# Revit family: Caja de conexión CBO 5-SEC_Aguilera Electronica
name_source: partatom
category: Equipos eléctricos
revit_build: Autodesk Revit 2017 (Build: 20160225_1515(x64)
units: mm (PartAtom-declared; Revit-internal decimal feet)

## family parameters
Anfitrión = Cara
Compartido = No
Corte con vacíos al cargar = No
Cota de conector redondo = Diámetro de uso
Número OmniClass = 23.85.30.21.11.14
Punto de cálculo de habitación = No
Tipo de pieza = Cuadro conmutador
Título OmniClass = Alarm Panels

## types (1)
- Caja de conexión CBO 5-SEC
    Alto = 130 mm  [stored 0.426509 ft]
    Ancho = 130 mm  [stored 0.426509 ft]
    Comentarios de tipo = Util para realizar la unión del cable de conexión CC15 con el cable de sensores y para derivaciones del cable de sensores.

Temperatura de trabajo: -35ºC a +60ºC (+80ºC en cortos periodos de tiempo).
Protección: IP 66
Dimensiones: 130x130x75mm
    Descripción = Caja para la conexión de un o dos cables sensor de temperatura tipo SEC15; incluye el módulo de conexión universal UCM.
Si no fuera posible conectar directamente el cable sensor a la unidad de control SCU800, se utiliza el cable de comunicación CC15 para la conexión del cable sensor a través de la caja de conexión a la unidad de control.
Se conectan en el interior de la caja de conexión el cable sensor con el cable de comunicación a través del módulo de conexión UCM.
El módulo de conexión universal UCM permite también la activación de la resistencia de adaptación de cada ramal en caso de configuración en estrella.
    Diámetro tubo = 15 mm  [stored 0.0492126 ft]
    Elevación por defecto = 1200 mm
    Fabricante = Aguilera Electrónica
    Fondo = 75 mm
    Modelo = AECS/CBO-SEC
    Símbolo = Sí
    Símbolo texto modelo = Sí
    URL = https://aguilera.es

note: [stored X ft] marks values corroborated as IEEE doubles in the binary element streams (Revit-internal decimal feet)
